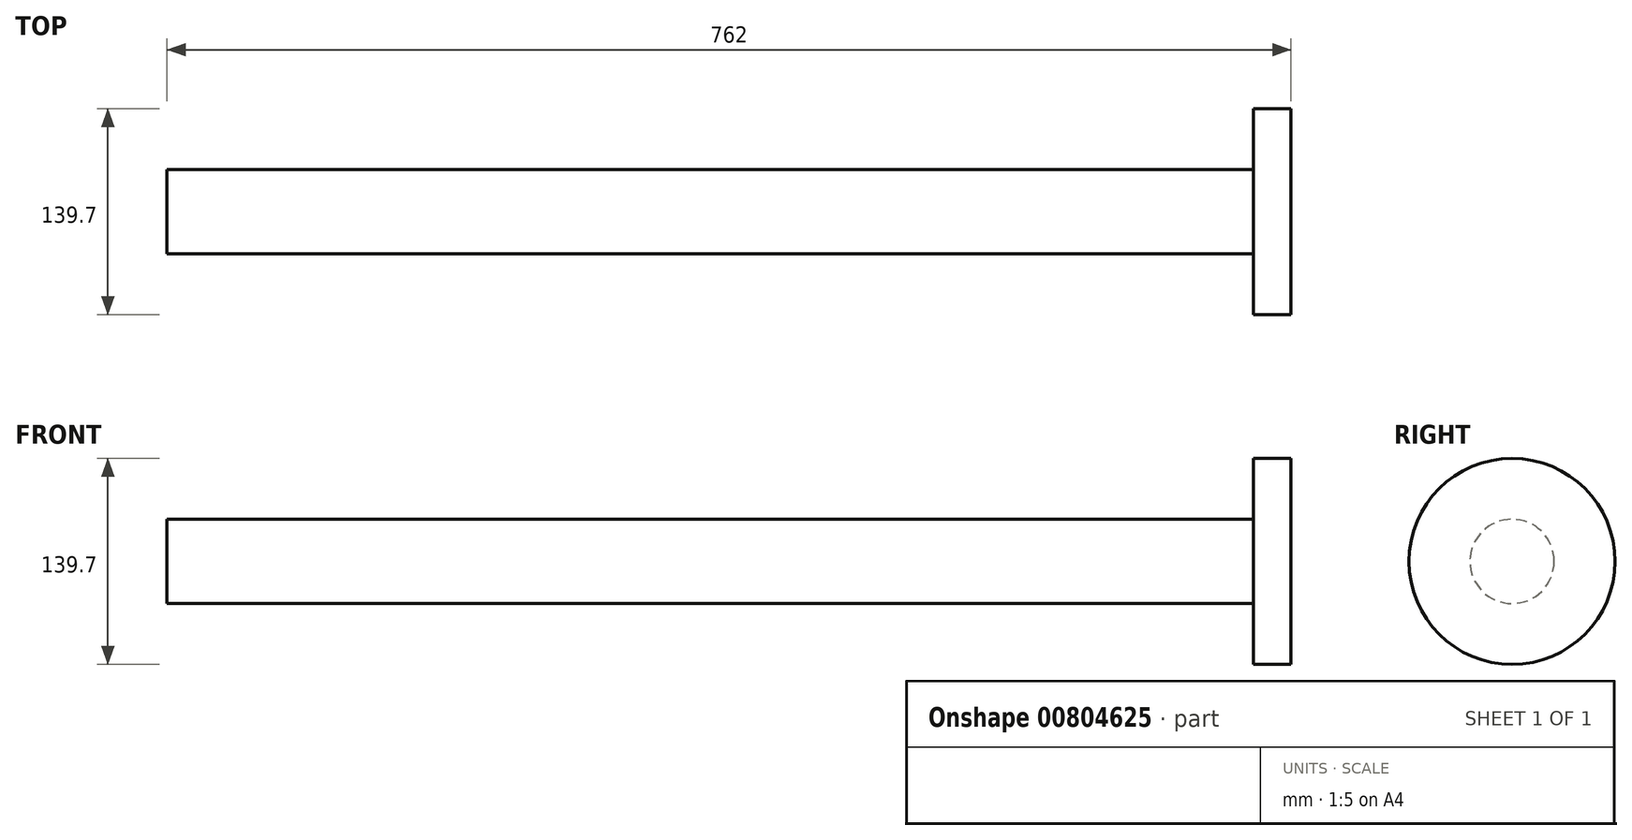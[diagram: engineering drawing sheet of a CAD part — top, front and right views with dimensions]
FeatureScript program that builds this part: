
annotation { "Feature Type Name" : "Feature", "Feature Type Description" : "" }
export const myFeature = defineFeature(function(context is Context, id is Id, definition is map)
    precondition{}
    {
        {
            var Q0;
            Q0=qCreatedBy(makeId("Right.planeOp"),FACE);
            var sketch = newSketch(context, id + "F0", { "sketchPlane" : qUnion([Q0])});
            skCircle(sketch, "E0", {"center": v(0, 0) * mm, "radius": 69.85 * mm});
            skSolve(sketch);
        }
        {
            var Q0;
            Q0=makeQuery(id+"F0.imprint","IMPRINT",FACE,{"disambiguationData":[TD([[makeQuery(id+"F0.imprint","IMPRINT",EDGE,{"derivedFrom":sQuery(id+"F0.wireOp",EDGE,"E0")}),1.0]])]});
            extrude(context, id + "F1", {"entities" : qUnion([Q0]), "depth" : 25.4 * mm, "offsetDistance" : 25.4 * mm});
        }
        {
            var Q0;
            Q0=makeQuery(id+"F1.opExtrude","CAP_FACE",FACE,{"disambiguationData":[OSD([sQuery(id+"F0.wireOp",EDGE,"E0")])],"isStart":false});
            var sketch = newSketch(context, id + "F2", { "sketchPlane" : qUnion([Q0])});
            skCircle(sketch, "E1", {"center": v(0, 0) * mm, "radius": 28.58 * mm});
            skSolve(sketch);
        }
        {
            var Q0;
            Q0=makeQuery(id+"F2.imprint","IMPRINT",FACE,{"disambiguationData":[TD([[makeQuery(id+"F2.imprint","IMPRINT",EDGE,{"derivedFrom":sQuery(id+"F2.wireOp",EDGE,"E1")}),1.0]])]});
            extrude(context, id + "F3", {"entities" : qUnion([Q0]), "operationType" : NewBodyOperationType.ADD, "oppositeDirection" : true, "depth" : 762 * mm, "offsetDistance" : 25.4 * mm});
        }
    });
